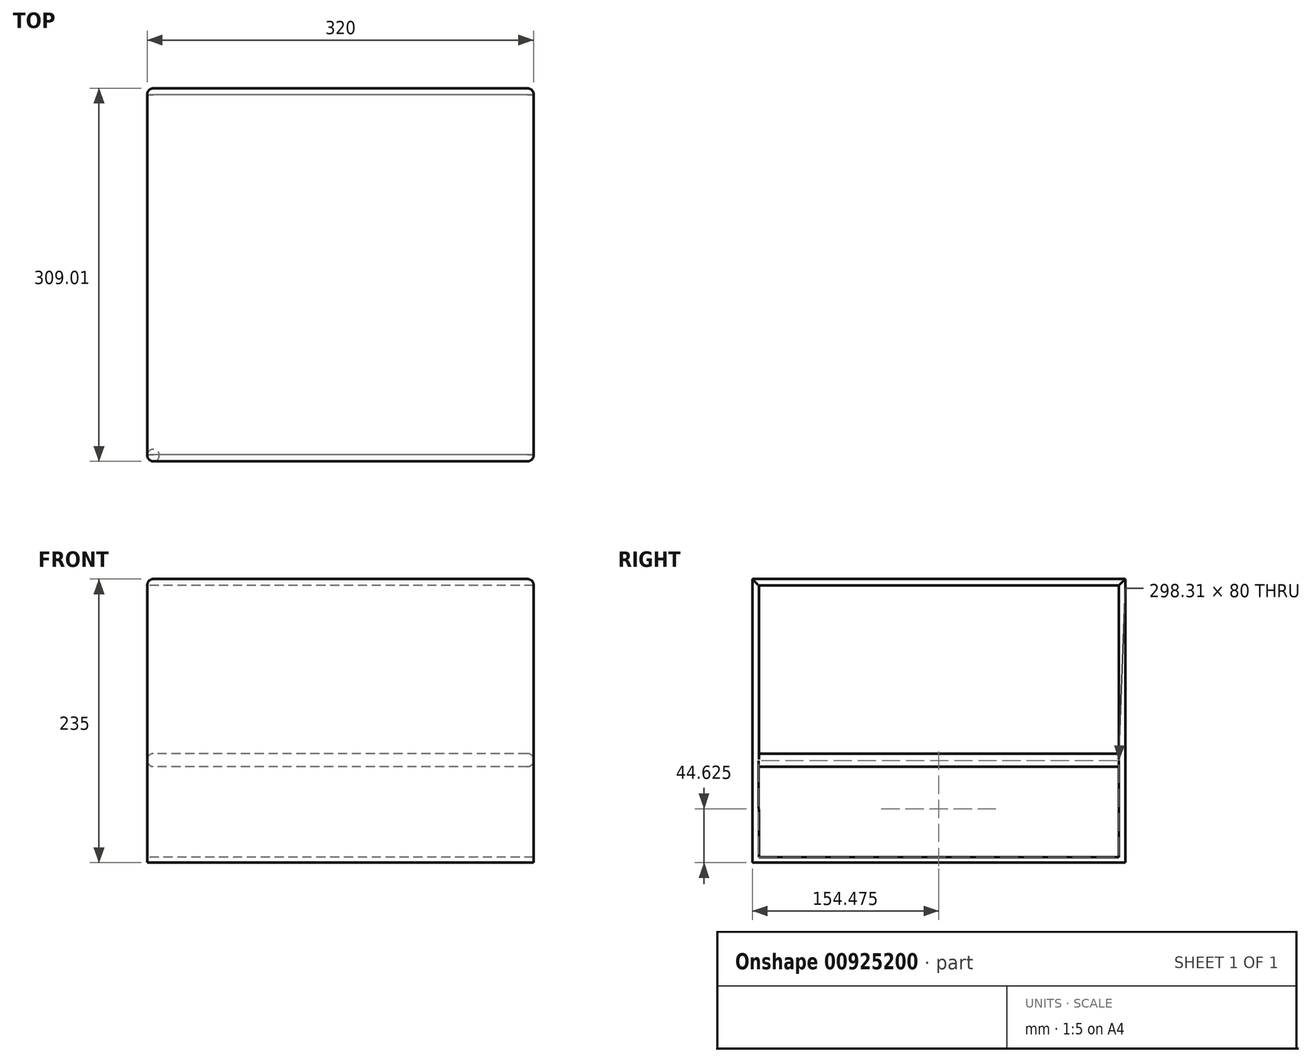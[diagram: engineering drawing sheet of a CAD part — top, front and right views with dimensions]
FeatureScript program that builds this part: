
annotation { "Feature Type Name" : "Feature", "Feature Type Description" : "" }
export const myFeature = defineFeature(function(context is Context, id is Id, definition is map)
    precondition{}
    {
        {
            var Q0;
            Q0=qCreatedBy(makeId("Right.planeOp"),FACE);
            var sketch = newSketch(context, id + "F0", { "sketchPlane" : qUnion([Q0])});
            skLineSegment(sketch, "E0", {"start": v(-139, -85) * mm, "end": v(170, -85) * mm});
            skLineSegment(sketch, "E1", {"start": v(170, -85) * mm, "end": v(170, 0) * mm});
            skLineSegment(sketch, "E2", {"start": v(170, 0) * mm, "end": v(-139, 0) * mm});
            skLineSegment(sketch, "E3", {"start": v(-139, 0) * mm, "end": v(-139, -85) * mm});
            skLineSegment(sketch, "E4", {"start": v(-133.55, -80.37) * mm, "end": v(164.62, -80.38) * mm});
            skLineSegment(sketch, "E5", {"start": v(164.62, -80.38) * mm, "end": v(164.62, -5.38) * mm});
            skLineSegment(sketch, "E6", {"start": v(-133.55, -80.37) * mm, "end": v(-133.68, -5.38) * mm});
            skLineSegment(sketch, "E7", {"start": v(164.62, -5.38) * mm, "end": v(-133.68, -5.38) * mm});
            skLineSegment(sketch, "E8", {"start": v(-139, 0) * mm, "end": v(-139, 150) * mm});
            skLineSegment(sketch, "E9", {"start": v(-139, 150) * mm, "end": v(170, 150) * mm});
            skLineSegment(sketch, "E10", {"start": v(170, 0) * mm, "end": v(170, 150) * mm});
            skLineSegment(sketch, "E11", {"start": v(164.62, 5.38) * mm, "end": v(164.62, 144.62) * mm});
            skLineSegment(sketch, "E12", {"start": v(164.62, 144.62) * mm, "end": v(-133.63, 144.62) * mm});
            skLineSegment(sketch, "E13", {"start": v(-133.63, 144.62) * mm, "end": v(-133.63, 5.38) * mm});
            skLineSegment(sketch, "E14", {"start": v(-133.63, 5.38) * mm, "end": v(164.62, 5.38) * mm});
            skLineSegment(sketch, "E15", {"start": v(50.74, -5.38) * mm, "end": v(50.74, 0) * mm});
            skLineSegment(sketch, "E16", {"start": v(50.74, 0) * mm, "end": v(50.74, 5.38) * mm});
            skSolve(sketch);
        }
        {
            var Q0;
            Q0=makeQuery(id+"F0.imprint","IMPRINT",FACE,{"disambiguationData":[TD([[makeQuery(id+"F0.imprint","IMPRINT",EDGE,{"derivedFrom":sQuery(id+"F0.wireOp",EDGE,"E2")}),-1.0]])]});
            var Q1;
            Q1=makeQuery(id+"F0.imprint","IMPRINT",FACE,{"disambiguationData":[TD([[makeQuery(id+"F0.imprint","IMPRINT",EDGE,{"derivedFrom":sQuery(id+"F0.wireOp",EDGE,"E0")}),1.0]])]});
            extrude(context, id + "F1", {"entities" : qUnion([Q0, Q1]), "depth" : 320 * mm, "offsetDistance" : 25 * mm});
        }
        {
            var Q0;
            Q0=makeQuery(id+"F1.opExtrude","CAP_EDGE",EDGE,{"disambiguationData":[OSD([sQuery(id+"F0.wireOp",EDGE,"E8")])],"isStart":false});
            var Q1;
            Q1=makeQuery(id+"F1.opExtrude","CAP_EDGE",EDGE,{"disambiguationData":[OSD([sQuery(id+"F0.wireOp",EDGE,"E3")])],"isStart":false});
            var Q2;
            Q2=makeQuery(id+"F1.opExtrude","CAP_EDGE",EDGE,{"disambiguationData":[OSD([sQuery(id+"F0.wireOp",EDGE,"E1")])],"isStart":false});
            var Q3;
            Q3=makeQuery(id+"F1.opExtrude","CAP_EDGE",EDGE,{"disambiguationData":[OSD([sQuery(id+"F0.wireOp",EDGE,"E10")])],"isStart":false});
            var Q4;
            Q4=makeQuery(id+"F1.opExtrude","CAP_EDGE",EDGE,{"disambiguationData":[OSD([sQuery(id+"F0.wireOp",EDGE,"E3")])],"isStart":true});
            var Q5;
            Q5=makeQuery(id+"F1.opExtrude","CAP_EDGE",EDGE,{"disambiguationData":[OSD([sQuery(id+"F0.wireOp",EDGE,"E8")])],"isStart":true});
            var Q6;
            Q6=makeQuery(id+"F1.opExtrude","CAP_EDGE",EDGE,{"disambiguationData":[OSD([sQuery(id+"F0.wireOp",EDGE,"E1")])],"isStart":true});
            var Q7;
            Q7=makeQuery(id+"F1.opExtrude","CAP_EDGE",EDGE,{"disambiguationData":[OSD([sQuery(id+"F0.wireOp",EDGE,"E10")])],"isStart":true});
            var Q8;
            Q8=makeQuery(id+"F1.opExtrude","CAP_EDGE",EDGE,{"disambiguationData":[OSD([sQuery(id+"F0.wireOp",EDGE,"E9")])],"isStart":true});
            var Q9;
            Q9=makeQuery(id+"F1.opExtrude","CAP_EDGE",EDGE,{"disambiguationData":[OSD([sQuery(id+"F0.wireOp",EDGE,"E9")])],"isStart":false});
            var Q10;
            Q10=makeQuery(id+"F1.opExtrude","CAP_EDGE",EDGE,{"disambiguationData":[OSD([sQuery(id+"F0.wireOp",EDGE,"E14")])],"isStart":false});
            var Q11;
            Q11=makeQuery(id+"F1.opExtrude","CAP_EDGE",EDGE,{"disambiguationData":[OSD([sQuery(id+"F0.wireOp",EDGE,"E7")])],"isStart":false});
            var Q12;
            Q12=makeQuery(id+"F1.opExtrude","CAP_EDGE",EDGE,{"disambiguationData":[OSD([sQuery(id+"F0.wireOp",EDGE,"E14")])],"isStart":true});
            var Q13;
            Q13=makeQuery(id+"F1.opExtrude","CAP_EDGE",EDGE,{"disambiguationData":[OSD([sQuery(id+"F0.wireOp",EDGE,"E7")])],"isStart":true});
            fillet(context, id + "F2", {"entities" : qUnion([Q0, Q1, Q2, Q3, Q4, Q5, Q6, Q7, Q8, Q9, Q10, Q11, Q12, Q13]), "radius" : 5 * mm, "tangentPropagation" : true, "allowEdgeOverflow" : false});
        }
    });
